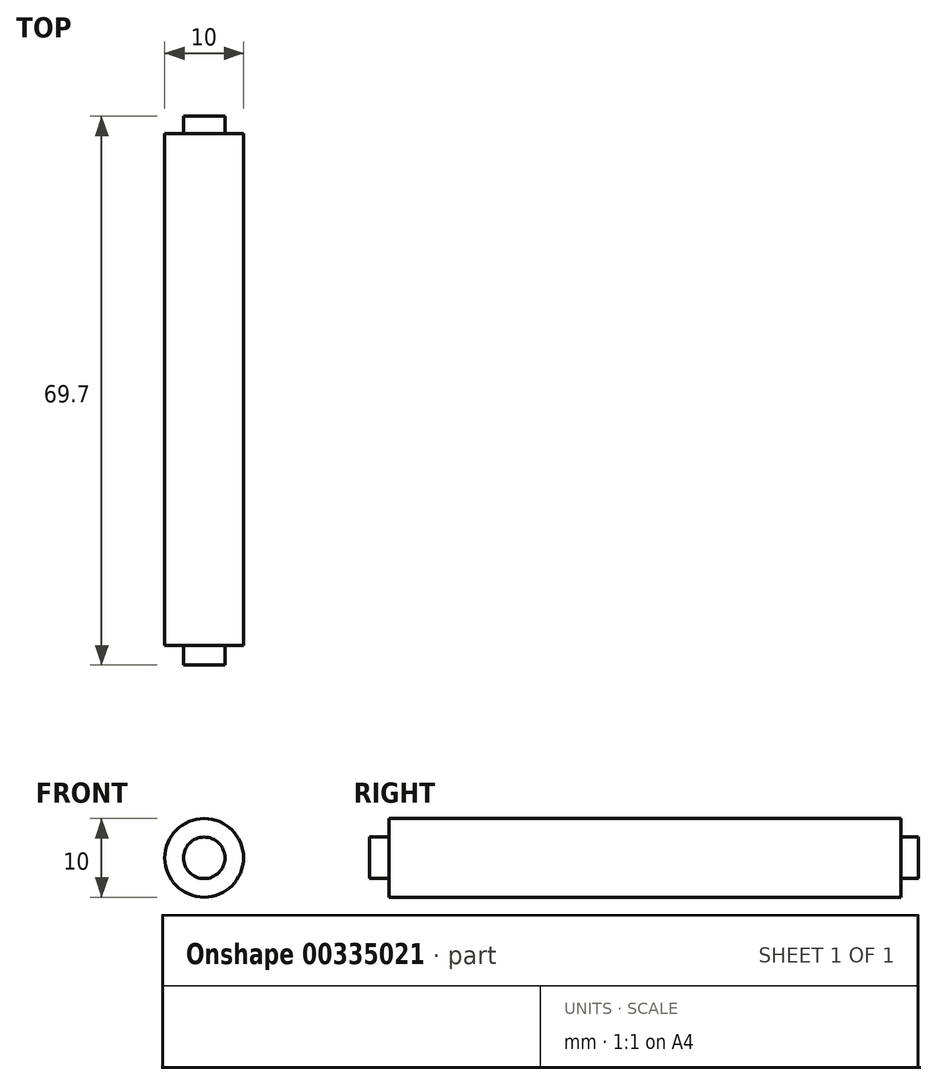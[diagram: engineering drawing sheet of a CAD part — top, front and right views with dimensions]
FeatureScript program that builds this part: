
annotation { "Feature Type Name" : "Feature", "Feature Type Description" : "" }
export const myFeature = defineFeature(function(context is Context, id is Id, definition is map)
    precondition{}
    {
        {
            var Q0;
            Q0=qCreatedBy(makeId("Front.planeOp"),FACE);
            var sketch = newSketch(context, id + "F0", { "sketchPlane" : qUnion([Q0])});
            skCircle(sketch, "E0", {"center": v(0, 0) * mm, "radius": 5 * mm});
            skSolve(sketch);
        }
        {
            var Q0;
            Q0=makeQuery(id+"F0.imprint","IMPRINT",FACE,{"disambiguationData":[TD([[makeQuery(id+"F0.imprint","IMPRINT",EDGE,{"derivedFrom":sQuery(id+"F0.wireOp",EDGE,"E0")}),1.0]])]});
            extrude(context, id + "F1", {"entities" : qUnion([Q0]), "depth" : 65 * mm});
        }
        {
            var Q0;
            Q0=makeQuery(id+"F1.opExtrude","CAP_FACE",FACE,{"disambiguationData":[OSD([sQuery(id+"F0.wireOp",EDGE,"E0")])],"isStart":false});
            var sketch = newSketch(context, id + "F2", { "sketchPlane" : qUnion([Q0])});
            skCircle(sketch, "E1", {"center": v(0, 0) * mm, "radius": 2.64 * mm});
            skSolve(sketch);
        }
        {
            var Q0;
            Q0=makeQuery(id+"F2.imprint","IMPRINT",FACE,{"disambiguationData":[TD([[makeQuery(id+"F2.imprint","IMPRINT",EDGE,{"derivedFrom":sQuery(id+"F2.wireOp",EDGE,"E1")}),1.0]])]});
            extrude(context, id + "F3", {"entities" : qUnion([Q0]), "operationType" : NewBodyOperationType.ADD, "depth" : 2.5 * mm, "hasSecondDirection" : true, "secondDirectionOppositeDirection" : true, "secondDirectionDepth" : 67.2 * mm});
        }
    });
